# Revit family: Flashing_Preformed_Hyload_Outside135
name_source: partatom
category: Generic Models
revit_build: Autodesk Revit 2014 (Build: 20130308_1515(x64)
units: mm (PartAtom-declared; Revit-internal decimal feet)

## types (1)
- As Specified
    Assembly Code = B3010400
    Construction Details = http://www.arcat.com
    Description = Preformed Hyload Masonry Flashing - Outside Corner (135)
    Flashing Material = Hyload Flashing Membrane - Grey
    Keynote = 07 65 00
    Manufacturer = Hyload
    Manufacturer Fax = 330-769-4153
    Manufacturer Website = http://www.hyload.com
    Model = Outside Corner (135)
    Product Data = http://www.arcat.com
    Product Properties = http://www.hyload.com
    Revision = R1_12-2015
    Sales Information = http://www.hyload.com
    Specification = http://www.arcat.com
    Thickness = 0' - 0 1/16"
    URL = http://www.hyload.com
    Unit Depth = 0' - 6"
    Unit Height = 0' - 6"
    Unit Width = 0' - 10"

## geometry (parser evidence)
native form markers: Blend x16, Sweep x1
no freeform markers — native parametric forms only
